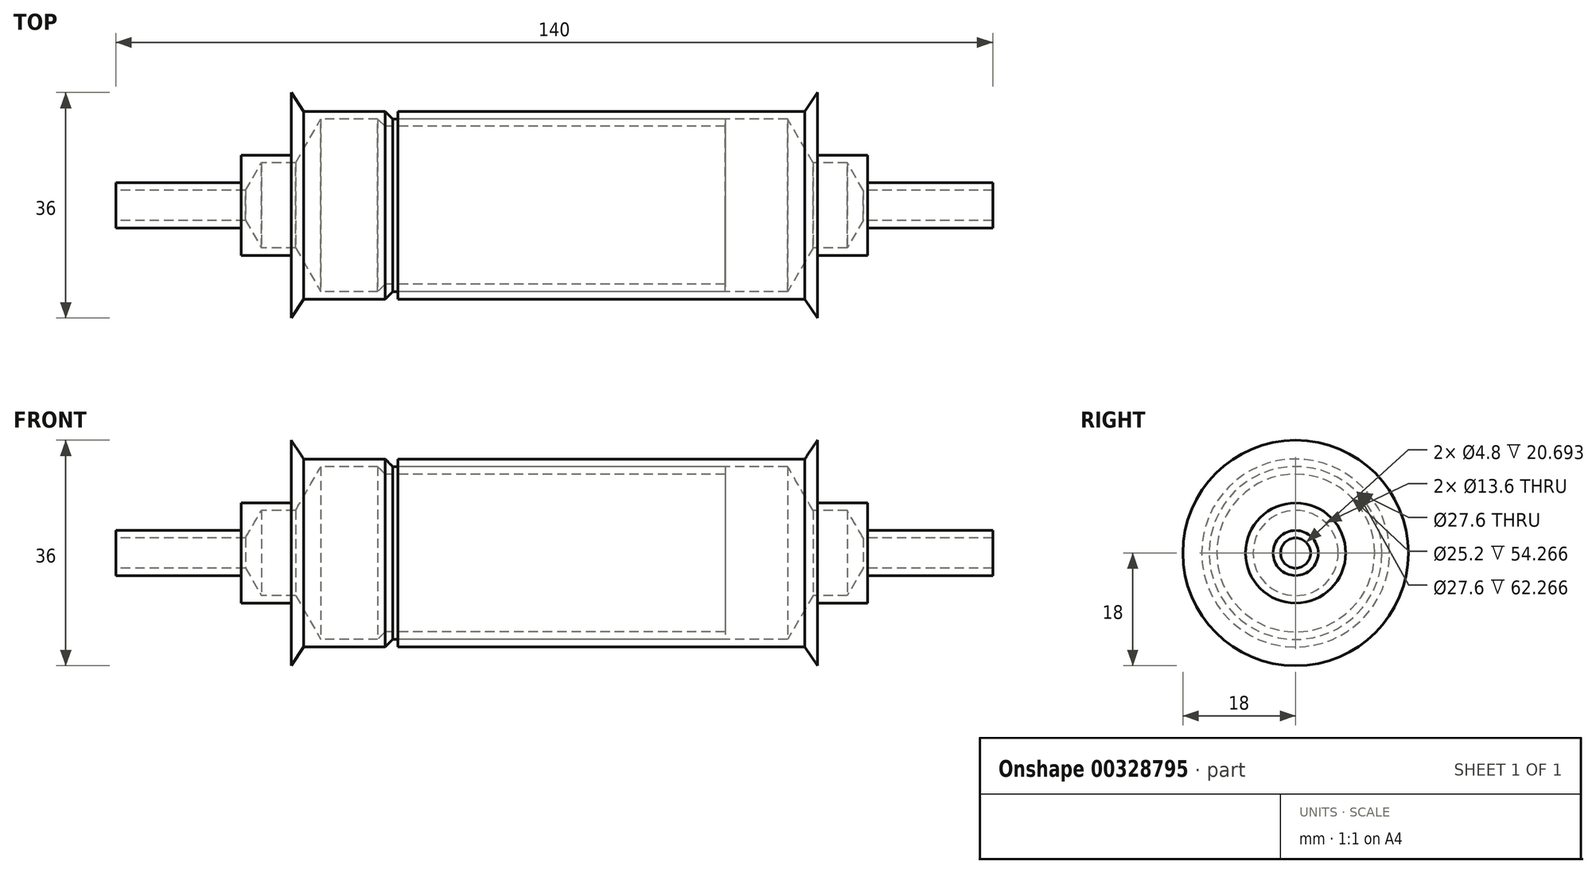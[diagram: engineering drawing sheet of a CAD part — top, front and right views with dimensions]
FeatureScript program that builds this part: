
annotation { "Feature Type Name" : "Feature", "Feature Type Description" : "" }
export const myFeature = defineFeature(function(context is Context, id is Id, definition is map)
    precondition{}
    {
        {
            var Q0;
            Q0=qCreatedBy(makeId("Front.planeOp"),FACE);
            var sketch = newSketch(context, id + "F0", { "sketchPlane" : qUnion([Q0])});
            skLineSegment(sketch, "E0", {"start": v(70, 3.6) * mm, "end": v(50, 3.6) * mm});
            skLineSegment(sketch, "E1", {"start": v(50, 8) * mm, "end": v(42, 8) * mm});
            skLineSegment(sketch, "E2", {"start": v(42, 18) * mm, "end": v(40, 15) * mm});
            skLineSegment(sketch, "E3", {"start": v(40, 15) * mm, "end": v(-25, 15) * mm});
            skLineSegment(sketch, "E4", {"start": v(-25, 15) * mm, "end": v(-25, 13.8) * mm});
            skLineSegment(sketch, "E5", {"start": v(-25, 13.8) * mm, "end": v(37.27, 13.8) * mm});
            skLineSegment(sketch, "E6", {"start": v(49.3, 2.4) * mm, "end": v(70, 2.4) * mm});
            skLineSegment(sketch, "E7", {"start": v(41.3, 6.8) * mm, "end": v(37.27, 13.8) * mm});
            skLineSegment(sketch, "E8", {"start": v(0, 0) * mm, "end": v(74.87, 0) * mm, "construction": true});
            skLineSegment(sketch, "E9", {"start": v(50, 8) * mm, "end": v(50, 3.6) * mm});
            skLineSegment(sketch, "E10", {"start": v(70, 3.6) * mm, "end": v(70, 2.4) * mm});
            skLineSegment(sketch, "E11", {"start": v(42, 8) * mm, "end": v(40.96, 7.4) * mm, "construction": true});
            skLineSegment(sketch, "E12", {"start": v(42, 8) * mm, "end": v(42, 18) * mm});
            skLineSegment(sketch, "E13", {"start": v(46.77, 6.8) * mm, "end": v(41.3, 6.8) * mm});
            skLineSegment(sketch, "E14", {"start": v(49.3, 2.4) * mm, "end": v(46.77, 6.8) * mm});
            skLineSegment(sketch, "E15", {"start": v(46.77, 6.8) * mm, "end": v(46.77, 8) * mm, "construction": true});
            skLineSegment(sketch, "E16", {"start": v(50, 3.6) * mm, "end": v(48.96, 3) * mm, "construction": true});
            skLineSegment(sketch, "E17.MirrorCS", {"start": v(-42, 18) * mm, "end": v(-40, 15) * mm, "construction": true});
            skSolve(sketch);
        }
        {
            var Q0;
            Q0=makeQuery(id+"F0.imprint","IMPRINT",FACE,{"disambiguationData":[TD([[makeQuery(id+"F0.imprint","IMPRINT",EDGE,{"derivedFrom":sQuery(id+"F0.wireOp",EDGE,"E0")}),1.0]])]});
            var Q1;
            Q1=sQuery(id+"F0.wireOp",EDGE,"E8");
            var Q2;
            Q2=sQuery(id+"F0.wireOp",EDGE,"E0");
            var Q3;
            Q3=sQuery(id+"F0.wireOp",EDGE,"asEibcgI-jTcl-GQX3-IyWU-w3ePdzjDX9v1");
            var Q4;
            Q4=sQuery(id+"F0.wireOp",EDGE,"E1");
            var Q5;
            Q5=sQuery(id+"F0.wireOp",EDGE,"39413bb7-427a-4a06-9a64-f9cf2ffad437.0");
            var Q6;
            Q6=sQuery(id+"F0.wireOp",EDGE,"E2");
            var Q7;
            Q7=sQuery(id+"F0.wireOp",EDGE,"E3");
            var Q8;
            Q8=sQuery(id+"F0.wireOp",EDGE,"E4");
            var Q9;
            Q9=sQuery(id+"F0.wireOp",EDGE,"E5");
            var Q10;
            Q10=sQuery(id+"F0.wireOp",EDGE,"E7");
            var Q11;
            Q11=sQuery(id+"F0.wireOp",EDGE,"E6");
            var Q12;
            Q12=sQuery(id+"F0.wireOp",EDGE,"b334028a-bd6f-4eda-a3a3-d9cde917d21f.0");
            var Q13;
            Q13=sQuery(id+"F0.wireOp",EDGE,"E8");
            revolve(context, id + "F1", {"entities" : qUnion([Q0]), "surfaceEntities" : qUnion([Q1, Q2, Q3, Q4, Q5, Q6, Q7, Q8, Q9, Q10, Q11, Q12]), "axis" : qUnion([Q13]), "revolveType" : RevolveType.FULL});
        }
        {
            var Q0;
            Q0=qCreatedBy(makeId("Front.planeOp"),FACE);
            var sketch = newSketch(context, id + "F2", { "sketchPlane" : qUnion([Q0])});
            skLineSegment(sketch, "E18.MirrorCS", {"start": v(-40, 15) * mm, "end": v(-27, 15) * mm});
            skLineSegment(sketch, "E19.MirrorCS", {"start": v(-28.2, 13.8) * mm, "end": v(-37.27, 13.8) * mm});
            skLineSegment(sketch, "E20.MirrorCS", {"start": v(-41.3, 6.8) * mm, "end": v(-37.27, 13.8) * mm});
            skLineSegment(sketch, "E21.MirrorCS", {"start": v(-40, 15) * mm, "end": v(-42, 18) * mm});
            skLineSegment(sketch, "E22.MirrorCS", {"start": v(-42, 8) * mm, "end": v(-42, 18) * mm});
            skLineSegment(sketch, "E23.MirrorCS", {"start": v(-42, 8) * mm, "end": v(-50, 8) * mm});
            skLineSegment(sketch, "E24.MirrorCS", {"start": v(-46.77, 6.8) * mm, "end": v(-41.3, 6.8) * mm});
            skLineSegment(sketch, "E25.MirrorCS", {"start": v(-46.77, 6.8) * mm, "end": v(-49.3, 2.4) * mm});
            skLineSegment(sketch, "E26.MirrorCS", {"start": v(-50, 3.6) * mm, "end": v(-50, 8) * mm});
            skLineSegment(sketch, "E27.MirrorCS", {"start": v(-50, 3.6) * mm, "end": v(-70, 3.6) * mm});
            skLineSegment(sketch, "E28.MirrorCS", {"start": v(-70, 2.4) * mm, "end": v(-49.3, 2.4) * mm});
            skLineSegment(sketch, "E29.MirrorCS", {"start": v(-70, 3.6) * mm, "end": v(-70, 2.4) * mm});
            skLineSegment(sketch, "E30", {"start": v(-50, 3.6) * mm, "end": v(-48.96, 3) * mm, "construction": true});
            skLineSegment(sketch, "E31", {"start": v(-42, 8) * mm, "end": v(-40.96, 7.4) * mm, "construction": true});
            skLineSegment(sketch, "E32", {"start": v(-46.77, 6.8) * mm, "end": v(-46.77, 8) * mm, "construction": true});
            skLineSegment(sketch, "E33", {"start": v(-27, 15) * mm, "end": v(-25.8, 13.8) * mm});
            skLineSegment(sketch, "E34", {"start": v(-28.2, 13.8) * mm, "end": v(-27, 12.6) * mm});
            skLineSegment(sketch, "E35", {"start": v(-25.8, 13.8) * mm, "end": v(27.27, 13.8) * mm});
            skLineSegment(sketch, "E36.MirrorCS", {"start": v(41.3, 6.8) * mm, "end": v(37.27, 13.8) * mm, "construction": true});
            skLineSegment(sketch, "E37", {"start": v(37.27, 13.8) * mm, "end": v(27.27, 13.8) * mm, "construction": true});
            skLineSegment(sketch, "E38", {"start": v(27.27, 13.8) * mm, "end": v(27.27, 12.6) * mm});
            skLineSegment(sketch, "E39", {"start": v(27.27, 12.6) * mm, "end": v(-27, 12.6) * mm});
            skLineSegment(sketch, "E40", {"start": v(-25.8, 13.8) * mm, "end": v(-27, 12.6) * mm});
            skLineSegment(sketch, "E41", {"start": v(-27, 15) * mm, "end": v(-28.2, 13.8) * mm});
            skSolve(sketch);
        }
        {
            var Q0;
            Q0=qSketchRegion(id+"F2",true);
            var Q1;
            Q1=sQuery(id+"F0.wireOp",EDGE,"E8");
            revolve(context, id + "F3", {"entities" : qUnion([Q0]), "axis" : qUnion([Q1]), "revolveType" : RevolveType.FULL});
        }
    });
